FCSTD DOCUMENT  (FreeCAD 0.20R26155 (Git))
Label: JS202011JCQN
License: All rights reserved
LicenseURL: http://en.wikipedia.org/wiki/All_rights_reserved
objects: Sketcher::SketchObject×1
note: 1 computed .brp shape members not serialized (recipe doc carries the construction recipe); baked Part::Feature solids carry a one-line shape summary decoded from their .brp

FEATURE [Sketcher::SketchObject] Sketch  label="Pads_TH_SMD"
  FullyConstrained = true
  sketch-geometry (32):
    g0: LineSegment StartX=-2.5 StartY=4 StartZ=0 EndX=-1.5 EndY=4 EndZ=0
    g1: LineSegment StartX=-1.5 StartY=4 StartZ=0 EndX=-1.5 EndY=2.4 EndZ=0
    g2: LineSegment StartX=-1.5 StartY=2.4 StartZ=0 EndX=-2.5 EndY=2.4 EndZ=0
    g3: LineSegment StartX=-2.5 StartY=2.4 StartZ=0 EndX=-2.5 EndY=4 EndZ=0
    g4: LineSegment StartX=0 StartY=4 StartZ=0 EndX=1 EndY=4 EndZ=0
    g5: LineSegment StartX=1 StartY=4 StartZ=0 EndX=1 EndY=2.4 EndZ=0
    g6: LineSegment StartX=1 StartY=2.4 StartZ=0 EndX=0 EndY=2.4 EndZ=0
    g7: LineSegment StartX=0 StartY=2.4 StartZ=0 EndX=0 EndY=4 EndZ=0
    g8: LineSegment StartX=2.5 StartY=4 StartZ=0 EndX=3.5 EndY=4 EndZ=0
    g9: LineSegment StartX=3.5 StartY=4 StartZ=0 EndX=3.5 EndY=2.4 EndZ=0
    g10: LineSegment StartX=3.5 StartY=2.4 StartZ=0 EndX=2.5 EndY=2.4 EndZ=0
    g11: LineSegment StartX=2.5 StartY=2.4 StartZ=0 EndX=2.5 EndY=4 EndZ=0
    g12: LineSegment StartX=-2.5 StartY=0 StartZ=0 EndX=-1.5 EndY=0 EndZ=0
    g13: LineSegment StartX=-1.5 StartY=0 StartZ=0 EndX=-1.5 EndY=1.6 EndZ=0
    g14: LineSegment StartX=-1.5 StartY=1.6 StartZ=0 EndX=-2.5 EndY=1.6 EndZ=0
    g15: LineSegment StartX=-2.5 StartY=1.6 StartZ=0 EndX=-2.5 EndY=0 EndZ=0
    g16: LineSegment StartX=0 StartY=0 StartZ=0 EndX=1 EndY=0 EndZ=0
    g17: LineSegment StartX=1 StartY=0 StartZ=0 EndX=1 EndY=1.6 EndZ=0
    g18: LineSegment StartX=1 StartY=1.6 StartZ=0 EndX=0 EndY=1.6 EndZ=0
    g19: LineSegment StartX=0 StartY=1.6 StartZ=0 EndX=0 EndY=0 EndZ=0
    g20: LineSegment StartX=2.5 StartY=0 StartZ=0 EndX=3.5 EndY=0 EndZ=0
    g21: LineSegment StartX=3.5 StartY=0 StartZ=0 EndX=3.5 EndY=1.6 EndZ=0
    g22: LineSegment StartX=3.5 StartY=1.6 StartZ=0 EndX=2.5 EndY=1.6 EndZ=0
    g23: LineSegment StartX=2.5 StartY=1.6 StartZ=0 EndX=2.5 EndY=0 EndZ=0
    g24: LineSegment StartX=-2.5 StartY=2.4 StartZ=0 EndX=3.5 EndY=2.4 EndZ=0
    g25: LineSegment StartX=-2.5 StartY=1.6 StartZ=0 EndX=3.5 EndY=1.6 EndZ=0
    g26: LineSegment StartX=-2 StartY=1.6 StartZ=0 EndX=-2 EndY=0 EndZ=0
    g27: LineSegment StartX=0.5 StartY=1.6 StartZ=0 EndX=0.5 EndY=0 EndZ=0
    g28: LineSegment StartX=3 StartY=1.6 StartZ=0 EndX=3 EndY=0 EndZ=0
    g29: LineSegment StartX=3 StartY=4 StartZ=0 EndX=3 EndY=2.4 EndZ=0
    g30: LineSegment StartX=0.5 StartY=4 StartZ=0 EndX=0.5 EndY=2.4 EndZ=0
    g31: LineSegment StartX=-2 StartY=4 StartZ=0 EndX=-2 EndY=2.4 EndZ=0
  constraints (93):
    c: Coincident(g0,g1)
    c: Coincident(g1,g2)
    c: Coincident(g2,g3)
    c: Coincident(g3,g0)
    c: Horizontal(g0)
    c: Horizontal(g2)
    c: Vertical(g1)
    c: Vertical(g3)
    c: Coincident(g4,g5)
    c: Coincident(g5,g6)
    c: Coincident(g6,g7)
    c: Coincident(g7,g4)
    c: Horizontal(g4)
    c: Horizontal(g6)
    c: Vertical(g5)
    c: Vertical(g7)
    c: PointOnObject(g4,g-2)
    c: Coincident(g8,g9)
    c: Coincident(g9,g10)
    c: Coincident(g10,g11)
    c: Coincident(g11,g8)
    c: Horizontal(g8)
    c: Horizontal(g10)
    c: Vertical(g9)
    c: Vertical(g11)
    c: Coincident(g12,g13)
    c: Coincident(g13,g14)
    c: Coincident(g14,g15)
    c: Coincident(g15,g12)
    c: Horizontal(g12)
    c: Horizontal(g14)
    c: Vertical(g13)
    c: Vertical(g15)
    c: PointOnObject(g12,g-1)
    c: Coincident(g16,g17)
    c: Coincident(g17,g18)
    c: Coincident(g18,g19)
    c: Coincident(g19,g16)
    c: Horizontal(g16)
    c: Horizontal(g18)
    c: Vertical(g17)
    c: Vertical(g19)
    c: Coincident(g16,g-1)
    c: Coincident(g20,g21)
    c: Coincident(g21,g22)
    c: Coincident(g22,g23)
    c: Coincident(g23,g20)
    c: Horizontal(g20)
    c: Horizontal(g22)
    c: Vertical(g21)
    c: Vertical(g23)
    c: PointOnObject(g20,g-1)
    c: Equal(g0,g4)
    c: Equal(g4,g8)
    c: Equal(g8,g14)
    c: Equal(g14,g18)
    c: Equal(g18,g22)
    c: DistanceX(g14,g14) = 1
    c: DistanceY(g12,g0) = 4
    c: DistanceY(g14,g2) = 0.8
    c: Equal(g3,g15)
    c: Equal(g15,g7)
    c: Equal(g7,g19)
    c: Equal(g19,g11)
    c: Equal(g11,g23)
    c: Coincident(g24,g2)
    c: Horizontal(g24)
    c: Coincident(g25,g14)
    c: Coincident(g25,g21)
    c: Coincident(g24,g9)
    c: PointOnObject(g5,g24)
    c: PointOnObject(g28,g22)
    c: PointOnObject(g28,g20)
    c: PointOnObject(g29,g8)
    c: PointOnObject(g29,g10)
    c: PointOnObject(g30,g4)
    c: PointOnObject(g30,g6)
    c: PointOnObject(g31,g0)
    c: PointOnObject(g31,g2)
    c: PointOnObject(g26,g12)
    c: PointOnObject(g27,g16)
    c: PointOnObject(g26,g14)
    c: PointOnObject(g27,g18)
    c: Symmetric(g14,g13,g26)
    c: Symmetric(g18,g17,g27)
    c: Symmetric(g22,g21,g28)
    c: Symmetric(g8,g8,g29)
    c: Symmetric(g4,g4,g30)
    c: Symmetric(g0,g0,g31)
    c: DistanceX(g31,g30) = 2.5
    c: DistanceX(g30,g29) = 2.5
    c: DistanceX(g26,g27) = 2.5
    c: DistanceX(g27,g28) = 2.5
